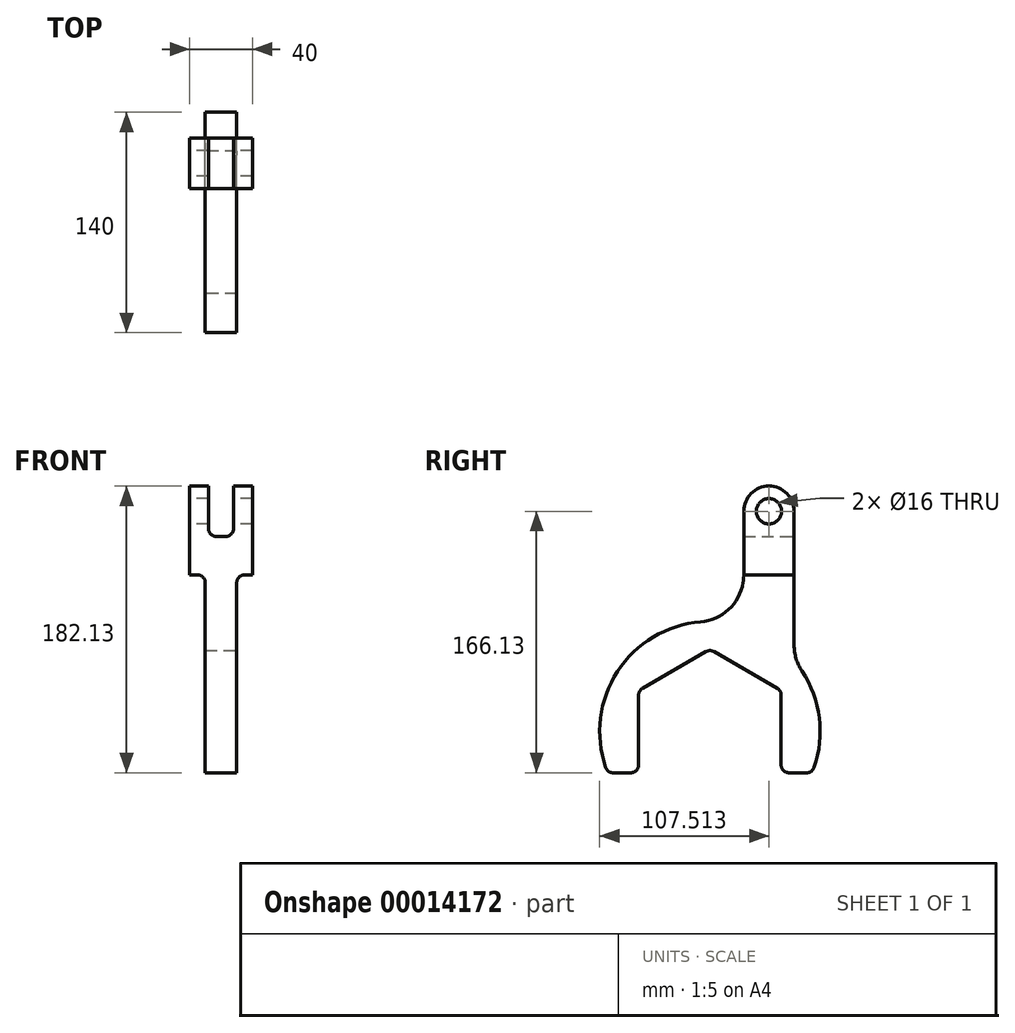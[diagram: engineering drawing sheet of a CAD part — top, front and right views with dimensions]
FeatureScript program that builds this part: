
annotation { "Feature Type Name" : "Feature", "Feature Type Description" : "" }
export const myFeature = defineFeature(function(context is Context, id is Id, definition is map)
    precondition{}
    {
        {
            var Q0;
            Q0=qCreatedBy(makeId("Right.planeOp"),FACE);
            var sketch = newSketch(context, id + "F0", { "sketchPlane" : qUnion([Q0])});
            skCircle(sketch, "E0.cCircle", {"center": v(0, 0) * mm, "radius": 45.25 * mm, "construction": true});
            skLineSegment(sketch, "E0.0", {"start": v(-45.25, -26.13) * mm, "end": v(-45.25, 26.13) * mm});
            skLineSegment(sketch, "E0.1", {"start": v(-45.25, 26.13) * mm, "end": v(0, 52.25) * mm});
            skLineSegment(sketch, "E0.2", {"start": v(0, 52.25) * mm, "end": v(45.25, 26.13) * mm});
            skLineSegment(sketch, "E0.3", {"start": v(45.25, 26.13) * mm, "end": v(45.25, -26.13) * mm});
            skLineSegment(sketch, "E0.4", {"start": v(22.63, -39.19) * mm, "end": v(21.51, -39.83) * mm});
            skPoint(sketch, "E0.0.midPoint", {"position": v(-45.25, 0) * mm});
            skLineSegment(sketch, "E1", {"start": v(0, 0) * mm, "end": v(0, 140) * mm, "construction": true});
            skLineSegment(sketch, "E2", {"start": v(0, 140) * mm, "end": v(132.53, 140) * mm, "construction": true});
            skLineSegment(sketch, "E3", {"start": v(0, 0) * mm, "end": v(37.51, 140) * mm, "construction": true});
            skCircle(sketch, "E4", {"center": v(37.51, 140) * mm, "radius": 8 * mm});
            skArc(sketch, "E5", {"start": v(53.51, 140) * mm, "mid": v(37.51, 156) * mm, "end": v(21.51, 140) * mm});
            skLineSegment(sketch, "E6", {"start": v(53.51, 140) * mm, "end": v(53.51, 55) * mm});
            skArc(sketch, "E7", {"start": v(64.94, -26.13) * mm, "mid": v(69.65, 6.99) * mm, "end": v(58.46, 38.5) * mm});
            skLineSegment(sketch, "E8", {"start": v(37.51, 140) * mm, "end": v(37.51, 210.9) * mm, "construction": true});
            skLineSegment(sketch, "E9.0.MirrorCS", {"start": v(21.51, 140) * mm, "end": v(21.51, 99.64) * mm});
            skLineSegment(sketch, "E10", {"start": v(-64.94, -26.13) * mm, "end": v(-45.25, -26.13) * mm});
            skPoint(sketch, "E11.orphan", {"position": v(53.51, -53.76) * mm});
            skArc(sketch, "E12.trimOffspring", {"start": v(-5.94, 69.75) * mm, "mid": v(-59.62, 36.69) * mm, "end": v(-64.94, -26.13) * mm});
            skPoint(sketch, "E13.orphan", {"position": v(-113.23, -26.13) * mm});
            skLineSegment(sketch, "E14.trimOffspring", {"start": v(45.25, -26.13) * mm, "end": v(64.94, -26.13) * mm});
            skPoint(sketch, "E15.visualSharp", {"position": v(53.51, 45.13) * mm});
            skArc(sketch, "E15.filletArc", {"start": v(53.51, 55) * mm, "mid": v(54.78, 46.4) * mm, "end": v(58.46, 38.5) * mm});
            skPoint(sketch, "E16.newPointA", {"position": v(21.51, -53.76) * mm});
            skArc(sketch, "E16.filletArc", {"start": v(-5.94, 69.75) * mm, "mid": v(13.6, 79.35) * mm, "end": v(21.51, 99.64) * mm});
            skSolve(sketch);
        }
        {
            var Q0;
            Q0 = qSketchRegion(id + "F0", true);
            extrude(context, id + "F1", {"entities" : qUnion([Q0]), "endBound" : BoundingType.SYMMETRIC, "depth" : 40 * mm});
        }
        {
            var Q0;
            Q0=makeQuery(id+"F1.opExtrude","CAP_FACE",FACE,{"disambiguationData":[OSD([sQuery(id+"F0.wireOp",EDGE,"E0.0"),sQuery(id+"F0.wireOp",EDGE,"E0.1"),sQuery(id+"F0.wireOp",EDGE,"E0.2"),sQuery(id+"F0.wireOp",EDGE,"E0.3"),sQuery(id+"F0.wireOp",EDGE,"E4"),sQuery(id+"F0.wireOp",EDGE,"E5"),sQuery(id+"F0.wireOp",EDGE,"E6"),sQuery(id+"F0.wireOp",EDGE,"E7"),sQuery(id+"F0.wireOp",EDGE,"E9.0.MirrorCS"),sQuery(id+"F0.wireOp",EDGE,"E10"),sQuery(id+"F0.wireOp",EDGE,"E12.trimOffspring"),sQuery(id+"F0.wireOp",EDGE,"E14.trimOffspring"),sQuery(id+"F0.wireOp",EDGE,"E15.filletArc"),sQuery(id+"F0.wireOp",EDGE,"E16.filletArc")])],"isStart":false});
            var sketch = newSketch(context, id + "F2", { "sketchPlane" : qUnion([Q0])});
            skArc(sketch, "E17.0", {"start": v(-5.94, 69.75) * mm, "mid": v(-59.62, 36.69) * mm, "end": v(-64.94, -26.13) * mm});
            skLineSegment(sketch, "E18.0", {"start": v(-64.94, -26.13) * mm, "end": v(-45.25, -26.13) * mm});
            skLineSegment(sketch, "E19.0", {"start": v(-45.25, -26.13) * mm, "end": v(-45.25, 26.13) * mm});
            skLineSegment(sketch, "E20.0", {"start": v(-45.25, 26.13) * mm, "end": v(0, 52.25) * mm});
            skLineSegment(sketch, "E21.0", {"start": v(0, 52.25) * mm, "end": v(45.25, 26.13) * mm});
            skLineSegment(sketch, "E22.0", {"start": v(45.25, 26.13) * mm, "end": v(45.25, -26.13) * mm});
            skLineSegment(sketch, "E23.0", {"start": v(45.25, -26.13) * mm, "end": v(64.94, -26.13) * mm});
            skArc(sketch, "E24.0", {"start": v(64.94, -26.13) * mm, "mid": v(69.65, 6.99) * mm, "end": v(58.46, 38.5) * mm});
            skArc(sketch, "E25.0", {"start": v(53.51, 55) * mm, "mid": v(54.78, 46.4) * mm, "end": v(58.46, 38.5) * mm});
            skArc(sketch, "E26.0", {"start": v(-5.94, 69.75) * mm, "mid": v(13.6, 79.35) * mm, "end": v(21.51, 99.64) * mm});
            skLineSegment(sketch, "E27.0", {"start": v(53.51, 140) * mm, "end": v(53.51, 55) * mm});
            skLineSegment(sketch, "E28", {"start": v(21.51, 99.64) * mm, "end": v(67.54, 99.64) * mm});
            skSolve(sketch);
        }
        {
            var Q0;
            Q0 = qSketchRegion(id + "F2", true);
            extrude(context, id + "F3", {"entities" : qUnion([Q0]), "operationType" : NewBodyOperationType.REMOVE, "oppositeDirection" : true, "depth" : 10 * mm});
        }
        {
            var Q0;
            Q0=makeQuery(id+"F1.opExtrude","CAP_FACE",FACE,{"disambiguationData":[OSD([sQuery(id+"F0.wireOp",EDGE,"E0.0"),sQuery(id+"F0.wireOp",EDGE,"E0.1"),sQuery(id+"F0.wireOp",EDGE,"E0.2"),sQuery(id+"F0.wireOp",EDGE,"E0.3"),sQuery(id+"F0.wireOp",EDGE,"E4"),sQuery(id+"F0.wireOp",EDGE,"E5"),sQuery(id+"F0.wireOp",EDGE,"E6"),sQuery(id+"F0.wireOp",EDGE,"E7"),sQuery(id+"F0.wireOp",EDGE,"E9.0.MirrorCS"),sQuery(id+"F0.wireOp",EDGE,"E10"),sQuery(id+"F0.wireOp",EDGE,"E12.trimOffspring"),sQuery(id+"F0.wireOp",EDGE,"E14.trimOffspring"),sQuery(id+"F0.wireOp",EDGE,"E15.filletArc"),sQuery(id+"F0.wireOp",EDGE,"E16.filletArc")])],"isStart":true});
            var sketch = newSketch(context, id + "F4", { "sketchPlane" : qUnion([Q0])});
            skArc(sketch, "E29.0", {"start": v(5.94, 69.75) * mm, "mid": v(-13.6, 79.35) * mm, "end": v(-21.51, 99.64) * mm});
            skLineSegment(sketch, "E30.0", {"start": v(-21.51, 99.64) * mm, "end": v(-53.51, 99.64) * mm});
            skLineSegment(sketch, "E31.0", {"start": v(-53.51, 140) * mm, "end": v(-53.51, 55) * mm});
            skArc(sketch, "E32.0", {"start": v(-53.51, 55) * mm, "mid": v(-54.78, 46.4) * mm, "end": v(-58.46, 38.5) * mm});
            skArc(sketch, "E33.0", {"start": v(-64.94, -26.13) * mm, "mid": v(-69.65, 6.99) * mm, "end": v(-58.46, 38.5) * mm});
            skLineSegment(sketch, "E34.0", {"start": v(-45.25, -26.13) * mm, "end": v(-64.94, -26.13) * mm});
            skLineSegment(sketch, "E35.0", {"start": v(-45.25, 26.13) * mm, "end": v(-45.25, -26.13) * mm});
            skLineSegment(sketch, "E36.0", {"start": v(0, 52.25) * mm, "end": v(-45.25, 26.13) * mm});
            skLineSegment(sketch, "E37.0", {"start": v(45.25, 26.13) * mm, "end": v(0, 52.25) * mm});
            skLineSegment(sketch, "E38.0", {"start": v(45.25, -26.13) * mm, "end": v(45.25, 26.13) * mm});
            skLineSegment(sketch, "E39.0", {"start": v(64.94, -26.13) * mm, "end": v(45.25, -26.13) * mm});
            skArc(sketch, "E40.0", {"start": v(5.94, 69.75) * mm, "mid": v(59.62, 36.69) * mm, "end": v(64.94, -26.13) * mm});
            skSolve(sketch);
        }
        {
            var Q0;
            Q0 = qSketchRegion(id + "F4", true);
            extrude(context, id + "F5", {"entities" : qUnion([Q0]), "operationType" : NewBodyOperationType.REMOVE, "oppositeDirection" : true, "depth" : 10 * mm});
        }
        {
            var Q0;
            Q0=makeQuery(id+"F5.boolean.opBoolean","COPY",EDGE,{"derivedFrom":makeQuery(id+"F5.opExtrude","CAP_EDGE",EDGE,{"disambiguationData":[OSD([sQuery(id+"F4.wireOp",EDGE,"E30.0")])],"isStart":false})});
            var Q1;
            Q1=makeQuery(id+"F5.boolean.opBoolean","COPY",EDGE,{"derivedFrom":makeQuery(id+"F5.opExtrude","CAP_EDGE",EDGE,{"disambiguationData":[OSD([sQuery(id+"F4.wireOp",EDGE,"E30.0")])],"isStart":true})});
            var Q2;
            Q2=makeQuery(id+"F3.boolean.opBoolean","COPY",EDGE,{"derivedFrom":makeQuery(id+"F3.opExtrude","CAP_EDGE",EDGE,{"disambiguationData":[OSD([sQuery(id+"F2.wireOp",EDGE,"E28")])],"isStart":false})});
            var Q3;
            Q3=makeQuery(id+"F3.boolean.opBoolean","COPY",EDGE,{"derivedFrom":makeQuery(id+"F3.opExtrude","CAP_EDGE",EDGE,{"disambiguationData":[OSD([sQuery(id+"F2.wireOp",EDGE,"E28")])],"isStart":true})});
            fillet(context, id + "F6", {"entities" : qUnion([Q0, Q1, Q2, Q3]), "radius" : 5 * mm, "tangentPropagation" : true, "allowEdgeOverflow" : false});
        }
        {
            var Q0;
            Q0=makeQuery(id+"F1.opExtrude","SWEPT_EDGE",EDGE,{"disambiguationData":[OSD([sQuery(id+"F0.wireOp",EDGE,"E0.3"),sQuery(id+"F0.wireOp",EDGE,"E14.trimOffspring")])]});
            var Q1;
            Q1=makeQuery(id+"F1.opExtrude","SWEPT_EDGE",EDGE,{"disambiguationData":[OSD([sQuery(id+"F0.wireOp",EDGE,"E0.0"),sQuery(id+"F0.wireOp",EDGE,"E10")])]});
            var Q2;
            Q2=makeQuery(id+"F1.opExtrude","SWEPT_EDGE",EDGE,{"disambiguationData":[OSD([sQuery(id+"F0.wireOp",EDGE,"E10"),sQuery(id+"F0.wireOp",EDGE,"E12.trimOffspring")])]});
            var Q3;
            Q3=makeQuery(id+"F1.opExtrude","SWEPT_EDGE",EDGE,{"disambiguationData":[OSD([sQuery(id+"F0.wireOp",EDGE,"E7"),sQuery(id+"F0.wireOp",EDGE,"E14.trimOffspring")])]});
            fillet(context, id + "F7", {"entities" : qUnion([Q0, Q1, Q2, Q3]), "radius" : 5 * mm, "tangentPropagation" : true, "allowEdgeOverflow" : false});
        }
        {
            var Q0;
            Q0=makeQuery(id+"F1.opExtrude","SWEPT_EDGE",EDGE,{"disambiguationData":[OSD([sQuery(id+"F0.wireOp",EDGE,"E0.2"),sQuery(id+"F0.wireOp",EDGE,"E0.3")])]});
            var Q1;
            Q1=makeQuery(id+"F1.opExtrude","SWEPT_EDGE",EDGE,{"disambiguationData":[OSD([sQuery(id+"F0.wireOp",EDGE,"E0.1"),sQuery(id+"F0.wireOp",EDGE,"E0.2")])]});
            var Q2;
            Q2=makeQuery(id+"F1.opExtrude","SWEPT_EDGE",EDGE,{"disambiguationData":[OSD([sQuery(id+"F0.wireOp",EDGE,"E0.0"),sQuery(id+"F0.wireOp",EDGE,"E0.1")])]});
            fillet(context, id + "F8", {"entities" : qUnion([Q0, Q1, Q2]), "radius" : 5 * mm, "tangentPropagation" : true, "allowEdgeOverflow" : false});
        }
        {
            var Q0;
            Q0=makeQuery(id+"F1.opExtrude","SWEPT_FACE",FACE,{"disambiguationData":[OSD([sQuery(id+"F0.wireOp",EDGE,"E6")])]});
            var sketch = newSketch(context, id + "F9", { "sketchPlane" : qUnion([Q0])});
            skLineSegment(sketch, "E41", {"start": v(0, 181.36) * mm, "end": v(0, -58.54) * mm, "construction": true});
            skLineSegment(sketch, "E42", {"start": v(-20, 156) * mm, "end": v(20, 156) * mm, "construction": true});
            skLineSegment(sketch, "E43.0", {"start": v(-20, 140) * mm, "end": v(20, 140) * mm, "construction": true});
            skLineSegment(sketch, "E44.0.MirrorCS", {"start": v(-20, 124) * mm, "end": v(20, 124) * mm, "construction": true});
            skLineSegment(sketch, "E45.0", {"start": v(-8, 181.36) * mm, "end": v(-8, -58.54) * mm, "construction": true});
            skLineSegment(sketch, "E46.0.MirrorCS", {"start": v(8, 181.36) * mm, "end": v(8, -58.54) * mm, "construction": true});
            skLineSegment(sketch, "E47.bottom", {"start": v(-8, 181.36) * mm, "end": v(8, 181.36) * mm});
            skLineSegment(sketch, "E47.top", {"start": v(-8, 124) * mm, "end": v(8, 124) * mm});
            skLineSegment(sketch, "E47.left", {"start": v(-8, 181.36) * mm, "end": v(-8, 124) * mm});
            skLineSegment(sketch, "E47.right", {"start": v(8, 181.36) * mm, "end": v(8, 124) * mm});
            skSolve(sketch);
        }
        {
            var Q0;
            Q0 = qSketchRegion(id + "F9", true);
            extrude(context, id + "F10", {"entities" : qUnion([Q0]), "operationType" : NewBodyOperationType.REMOVE, "endBound" : BoundingType.THROUGH_ALL, "oppositeDirection" : true, "depth" : 25 * mm});
        }
        {
            var Q0;
            Q0=makeQuery(id+"F10.boolean.opBoolean","COPY",EDGE,{"derivedFrom":makeQuery(id+"F10.opExtrude","SWEPT_EDGE",EDGE,{"disambiguationData":[OSD([sQuery(id+"F9.wireOp",EDGE,"E47.top"),sQuery(id+"F9.wireOp",EDGE,"E47.left")])]})});
            var Q1;
            Q1=makeQuery(id+"F10.boolean.opBoolean","COPY",EDGE,{"derivedFrom":makeQuery(id+"F10.opExtrude","SWEPT_EDGE",EDGE,{"disambiguationData":[OSD([sQuery(id+"F9.wireOp",EDGE,"E47.top"),sQuery(id+"F9.wireOp",EDGE,"E47.right")])]})});
            fillet(context, id + "F11", {"entities" : qUnion([Q0, Q1]), "radius" : 5 * mm, "tangentPropagation" : true, "allowEdgeOverflow" : false});
        }
    });
